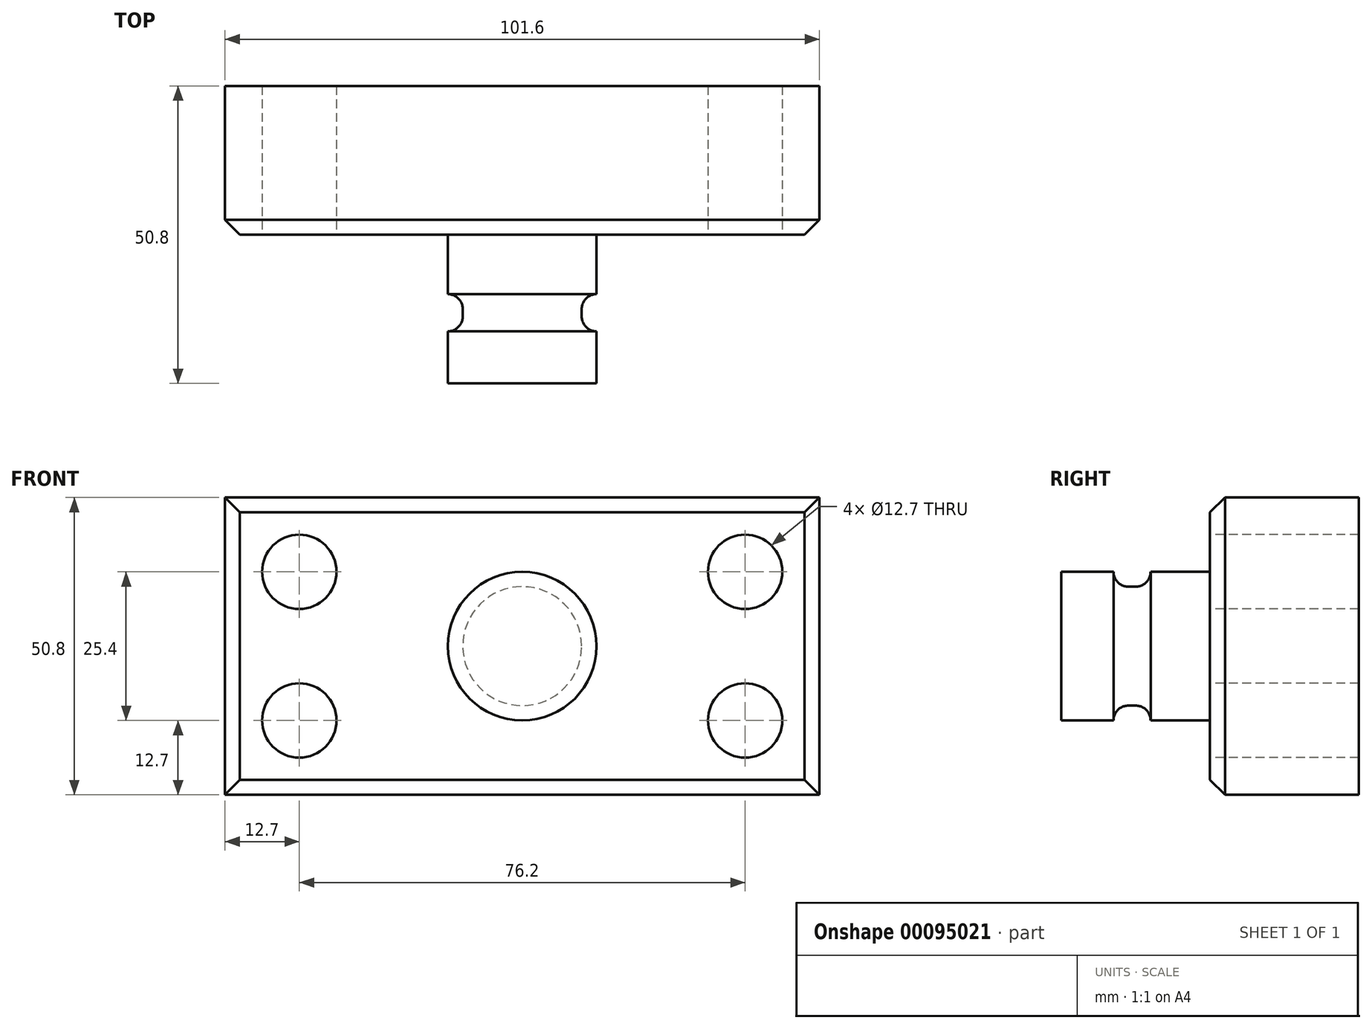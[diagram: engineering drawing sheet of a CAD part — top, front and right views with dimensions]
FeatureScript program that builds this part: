
annotation { "Feature Type Name" : "Feature", "Feature Type Description" : "" }
export const myFeature = defineFeature(function(context is Context, id is Id, definition is map)
    precondition{}
    {
        {
            var Q0;
            Q0=qCreatedBy(makeId("Front.planeOp"),FACE);
            var sketch = newSketch(context, id + "F0", { "sketchPlane" : qUnion([Q0])});
            skLineSegment(sketch, "E0.bottom", {"start": v(50.8, 25.4) * mm, "end": v(-50.8, 25.4) * mm});
            skLineSegment(sketch, "E0.top", {"start": v(50.8, -25.4) * mm, "end": v(-50.8, -25.4) * mm});
            skLineSegment(sketch, "E0.left", {"start": v(50.8, 25.4) * mm, "end": v(50.8, -25.4) * mm});
            skLineSegment(sketch, "E0.right", {"start": v(-50.8, 25.4) * mm, "end": v(-50.8, -25.4) * mm});
            skPoint(sketch, "E0.middle", {"position": v(0, 0) * mm});
            skSolve(sketch);
        }
        {
            var Q0;
            Q0 = qSketchRegion(id + "F0", true);
            extrude(context, id + "F1", {"entities" : qUnion([Q0]), "depth" : 25.4 * mm});
        }
        {
            var Q0;
            Q0=makeQuery(id+"F1.opExtrude","CAP_FACE",FACE,{"disambiguationData":[OSD([sQuery(id+"F0.wireOp",EDGE,"E0.bottom"),sQuery(id+"F0.wireOp",EDGE,"E0.top"),sQuery(id+"F0.wireOp",EDGE,"E0.left"),sQuery(id+"F0.wireOp",EDGE,"E0.right")])],"isStart":false});
            var sketch = newSketch(context, id + "F2", { "sketchPlane" : qUnion([Q0])});
            skCircle(sketch, "E1", {"center": v(-38.1, 12.7) * mm, "radius": 6.35 * mm});
            skCircle(sketch, "E2", {"center": v(-38.1, -12.7) * mm, "radius": 6.35 * mm});
            skCircle(sketch, "E3", {"center": v(38.1, 12.7) * mm, "radius": 6.35 * mm});
            skCircle(sketch, "E4", {"center": v(38.1, -12.7) * mm, "radius": 6.35 * mm});
            skSolve(sketch);
        }
        {
            var Q0;
            Q0 = qSketchRegion(id + "F2", true);
            extrude(context, id + "F3", {"entities" : qUnion([Q0]), "operationType" : NewBodyOperationType.REMOVE, "endBound" : BoundingType.THROUGH_ALL, "oppositeDirection" : true, "depth" : 25.4 * mm});
        }
        {
            var Q0;
            Q0=qCreatedBy(makeId("Top.planeOp"),FACE);
            var sketch = newSketch(context, id + "F4", { "sketchPlane" : qUnion([Q0])});
            skLineSegment(sketch, "E5.bottom", {"start": v(0, -25.4) * mm, "end": v(-12.7, -25.4) * mm});
            skLineSegment(sketch, "E5.top", {"start": v(0, -50.8) * mm, "end": v(-12.7, -50.8) * mm});
            skLineSegment(sketch, "E5.left", {"start": v(0, -25.4) * mm, "end": v(0, -50.8) * mm});
            skLineSegment(sketch, "E5.right", {"start": v(-12.7, -25.4) * mm, "end": v(-12.7, -50.8) * mm});
            skSolve(sketch);
        }
        {
            var Q0;
            Q0 = qSketchRegion(id + "F4", true);
            var Q1;
            Q1=sQuery(id+"F4.wireOp",EDGE,"E5.left");
            revolve(context, id + "F5", {"operationType" : NewBodyOperationType.ADD, "entities" : qUnion([Q0]), "axis" : qUnion([Q1]), "revolveType" : RevolveType.FULL});
        }
        {
            var Q0;
            Q0=qCreatedBy(makeId("Top.planeOp"),FACE);
            var sketch = newSketch(context, id + "F6", { "sketchPlane" : qUnion([Q0])});
            skLineSegment(sketch, "E6.bottom", {"start": v(22.24, -41.91) * mm, "end": v(10.16, -41.91) * mm});
            skLineSegment(sketch, "E6.top", {"start": v(22.24, -35.56) * mm, "end": v(10.16, -35.56) * mm});
            skLineSegment(sketch, "E6.left", {"start": v(22.24, -41.91) * mm, "end": v(22.24, -35.56) * mm});
            skLineSegment(sketch, "E6.right", {"start": v(10.16, -41.91) * mm, "end": v(10.16, -35.56) * mm});
            skLineSegment(sketch, "E7", {"start": v(0, 0) * mm, "end": v(0, -80.67) * mm, "construction": true});
            skSolve(sketch);
        }
        {
            var Q0;
            Q0 = qSketchRegion(id + "F6", true);
            var Q1;
            Q1=sQuery(id+"F6.wireOp",EDGE,"E7");
            revolve(context, id + "F7", {"operationType" : NewBodyOperationType.REMOVE, "entities" : qUnion([Q0]), "axis" : qUnion([Q1]), "revolveType" : RevolveType.FULL, "oppositeDirection" : true});
        }
        {
            var Q0;
            Q0=makeQuery(id+"F5.opRevolve","SWEPT_EDGE",EDGE,{"disambiguationData":[OSD([sQuery(id+"F4.wireOp",EDGE,"E5.bottom"),sQuery(id+"F4.wireOp",EDGE,"E5.right")])]});
            var Q1;
            Q1=makeQuery(id+"F7.boolean.opBoolean","COPY",EDGE,{"derivedFrom":makeQuery(id+"F7.opRevolve","SWEPT_EDGE",EDGE,{"disambiguationData":[OSD([sQuery(id+"F6.wireOp",EDGE,"E6.bottom"),sQuery(id+"F6.wireOp",EDGE,"E6.right")])]})});
            var Q2;
            Q2=makeQuery(id+"F7.boolean.opBoolean","COPY",EDGE,{"derivedFrom":makeQuery(id+"F7.opRevolve","SWEPT_EDGE",EDGE,{"disambiguationData":[OSD([sQuery(id+"F6.wireOp",EDGE,"E6.top"),sQuery(id+"F6.wireOp",EDGE,"E6.right")])]})});
            fillet(context, id + "F8", {"entities" : qUnion([Q0, Q1, Q2]), "radius" : 2.54 * mm, "tangentPropagation" : true, "allowEdgeOverflow" : false});
        }
        {
            var Q0;
            Q0=makeQuery(id+"F1.opExtrude","CAP_EDGE",EDGE,{"disambiguationData":[OSD([sQuery(id+"F0.wireOp",EDGE,"E0.bottom")])],"isStart":false});
            var Q1;
            Q1=makeQuery(id+"F1.opExtrude","CAP_EDGE",EDGE,{"disambiguationData":[OSD([sQuery(id+"F0.wireOp",EDGE,"E0.right")])],"isStart":false});
            var Q2;
            Q2=makeQuery(id+"F1.opExtrude","CAP_EDGE",EDGE,{"disambiguationData":[OSD([sQuery(id+"F0.wireOp",EDGE,"E0.top")])],"isStart":false});
            var Q3;
            Q3=makeQuery(id+"F1.opExtrude","CAP_EDGE",EDGE,{"disambiguationData":[OSD([sQuery(id+"F0.wireOp",EDGE,"E0.left")])],"isStart":false});
            chamfer(context, id + "F9", {"entities" : qUnion([Q0, Q1, Q2, Q3]), "width" : 2.54 * mm, "tangentPropagation" : true});
        }
    });
